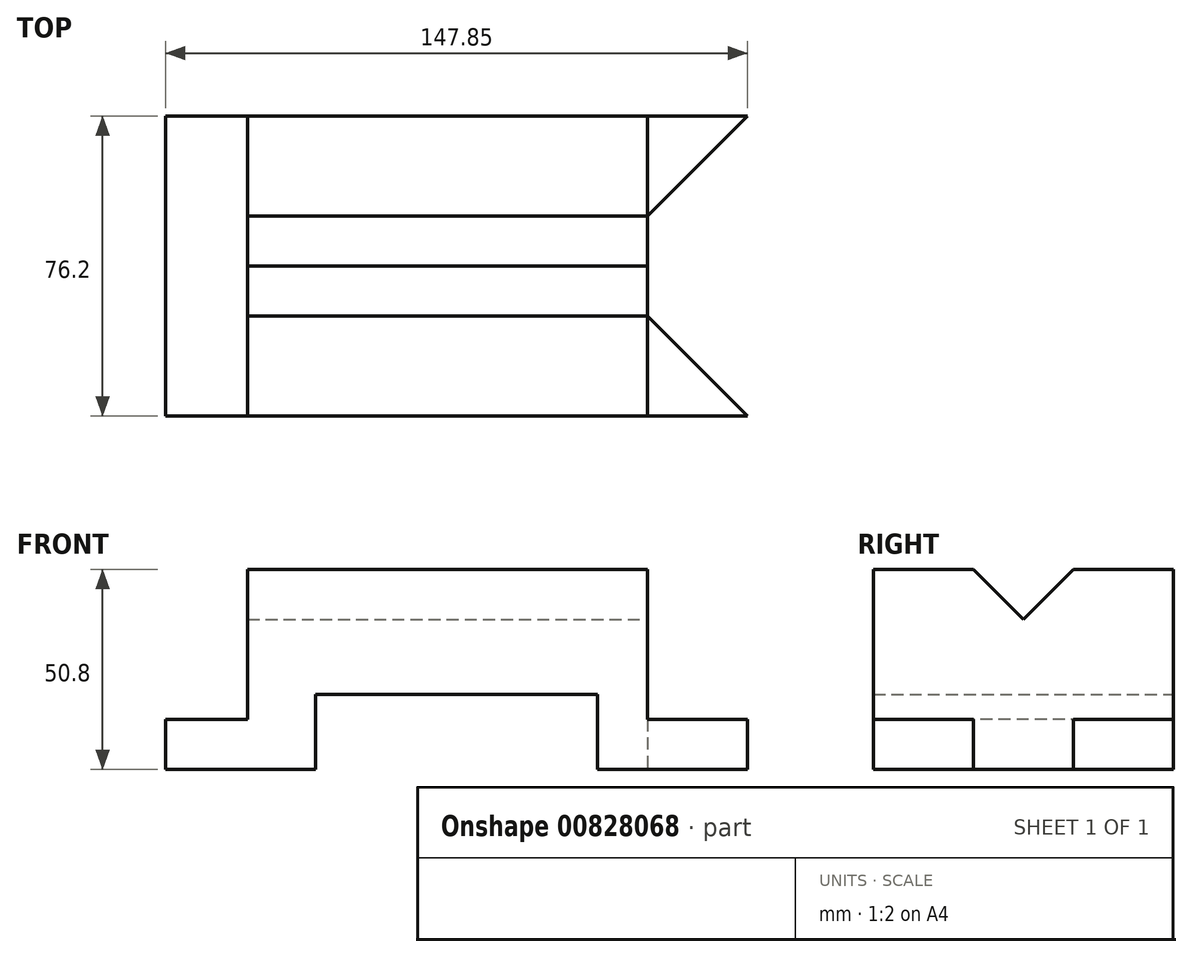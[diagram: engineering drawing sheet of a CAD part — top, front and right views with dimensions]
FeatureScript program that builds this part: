
annotation { "Feature Type Name" : "Feature", "Feature Type Description" : "" }
export const myFeature = defineFeature(function(context is Context, id is Id, definition is map)
    precondition{}
    {
        {
            var Q0;
            Q0=qCreatedBy(makeId("Top.planeOp"),FACE);
            var sketch = newSketch(context, id + "F0", { "sketchPlane" : qUnion([Q0])});
            skLineSegment(sketch, "E0", {"start": v(-51.86, 50.8) * mm, "end": v(-51.86, 54.53) * mm});
            skLineSegment(sketch, "E1", {"start": v(-51.86, 50.8) * mm, "end": v(-51.86, -25.4) * mm});
            skLineSegment(sketch, "E2", {"start": v(-51.86, -25.4) * mm, "end": v(49.74, -25.4) * mm});
            skLineSegment(sketch, "E3", {"start": v(49.74, -25.4) * mm, "end": v(49.74, 50.8) * mm});
            skLineSegment(sketch, "E4", {"start": v(49.74, 50.8) * mm, "end": v(-51.86, 50.8) * mm});
            skLineSegment(sketch, "E5", {"start": v(49.74, -25.4) * mm, "end": v(75.14, -25.4) * mm});
            skLineSegment(sketch, "E6", {"start": v(75.14, -25.4) * mm, "end": v(49.74, 0) * mm});
            skLineSegment(sketch, "E7", {"start": v(49.74, 50.8) * mm, "end": v(75.14, 50.8) * mm});
            skLineSegment(sketch, "E8", {"start": v(75.14, 50.8) * mm, "end": v(49.74, 25.4) * mm});
            skLineSegment(sketch, "E9", {"start": v(-51.86, 50.8) * mm, "end": v(-72.71, 50.8) * mm});
            skLineSegment(sketch, "E10", {"start": v(-72.71, 50.8) * mm, "end": v(-72.71, -25.4) * mm});
            skLineSegment(sketch, "E11", {"start": v(-72.71, -25.4) * mm, "end": v(-51.86, -25.4) * mm});
            skSolve(sketch);
        }
        {
            var Q0;
            Q0=makeQuery(id+"F0.imprint","IMPRINT",FACE,{"disambiguationData":[TD([[makeQuery(id+"F0.imprint","IMPRINT",EDGE,{"derivedFrom":sQuery(id+"F0.wireOp",EDGE,"E1")}),-1.0]])]});
            extrude(context, id + "F1", {"entities" : qUnion([Q0]), "depth" : 12.7 * mm, "offsetDistance" : 25.4 * mm});
        }
        {
            var Q0;
            Q0=makeQuery(id+"F0.imprint","IMPRINT",FACE,{"disambiguationData":[TD([[makeQuery(id+"F0.imprint","IMPRINT",EDGE,{"derivedFrom":sQuery(id+"F0.wireOp",EDGE,"E1")}),1.0]])]});
            extrude(context, id + "F2", {"entities" : qUnion([Q0]), "operationType" : NewBodyOperationType.ADD, "depth" : 50.8 * mm, "offsetDistance" : 25.4 * mm});
        }
        {
            var Q0;
            {var subQ0=sQuery(id+"F0.wireOp",EDGE,"E7");Q0=makeQuery(id+"F0.imprint","IMPRINT",FACE,{"disambiguationData":[TD([[makeQuery(id+"F0.imprint","IMPRINT",EDGE,{"derivedFrom":subQ0}),-1.0]])]});}
            extrude(context, id + "F3", {"entities" : qUnion([Q0]), "operationType" : NewBodyOperationType.ADD, "depth" : 12.7 * mm, "offsetDistance" : 25.4 * mm});
        }
        {
            var Q0;
            {var subQ0=sQuery(id+"F0.wireOp",EDGE,"E5");Q0=makeQuery(id+"F0.imprint","IMPRINT",FACE,{"disambiguationData":[TD([[makeQuery(id+"F0.imprint","IMPRINT",EDGE,{"derivedFrom":subQ0}),1.0]])]});}
            extrude(context, id + "F4", {"entities" : qUnion([Q0]), "operationType" : NewBodyOperationType.ADD, "depth" : 12.7 * mm, "offsetDistance" : 25.4 * mm});
        }
        {
            var Q0;
            Q0=makeQuery(id+"F2.opExtrude","SWEPT_FACE",FACE,{"disambiguationData":[OSD([sQuery(id+"F0.wireOp",EDGE,"E3")])]});
            var sketch = newSketch(context, id + "F5", { "sketchPlane" : qUnion([Q0])});
            skLineSegment(sketch, "E12", {"start": v(0, 50.8) * mm, "end": v(12.7, 38.1) * mm});
            skLineSegment(sketch, "E13", {"start": v(12.7, 38.1) * mm, "end": v(25.4, 50.8) * mm});
            skSolve(sketch);
        }
        {
            var Q0;
            {var subQ0=sQuery(id+"F5.wireOp",EDGE,"E12");Q0=makeQuery(id+"F5.imprint","IMPRINT",FACE,{"disambiguationData":[TD([[makeQuery(id+"F5.imprint","IMPRINT",EDGE,{"derivedFrom":subQ0}),1.0]])]});}
            extrude(context, id + "F6", {"entities" : qUnion([Q0]), "operationType" : NewBodyOperationType.REMOVE, "endBound" : BoundingType.THROUGH_ALL, "oppositeDirection" : true, "depth" : 25.4 * mm, "offsetDistance" : 25.4 * mm});
        }
        {
            var Q0;
            Q0=makeQuery(id+"F3.boolean.opBoolean","MERGE",FACE,{"derivedFrom":[makeQuery(id+"F2.boolean.opBoolean","MERGE",FACE,{"derivedFrom":[makeQuery(id+"F1.opExtrude","SWEPT_FACE",FACE,{"disambiguationData":[OSD([sQuery(id+"F0.wireOp",EDGE,"E9")])]}),makeQuery(id+"F2.opExtrude","SWEPT_FACE",FACE,{"disambiguationData":[OSD([sQuery(id+"F0.wireOp",EDGE,"E4")])]})]}),makeQuery(id+"F3.opExtrude","SWEPT_FACE",FACE,{"disambiguationData":[OSD([sQuery(id+"F0.wireOp",EDGE,"E7")])]})]});
            var sketch = newSketch(context, id + "F7", { "sketchPlane" : qUnion([Q0])});
            skLineSegment(sketch, "E14", {"start": v(-37.04, 0) * mm, "end": v(-37.04, 19.05) * mm});
            skLineSegment(sketch, "E15", {"start": v(34.61, 0) * mm, "end": v(34.61, 19.05) * mm});
            skLineSegment(sketch, "E16", {"start": v(-37.04, 19.05) * mm, "end": v(34.61, 19.05) * mm});
            skSolve(sketch);
        }
        {
            var Q0;
            {var subQ0=sQuery(id+"F7.wireOp",EDGE,"E14");Q0=makeQuery(id+"F7.imprint","IMPRINT",FACE,{"disambiguationData":[TD([[makeQuery(id+"F7.imprint","IMPRINT",EDGE,{"derivedFrom":subQ0}),-1.0]])]});}
            extrude(context, id + "F8", {"entities" : qUnion([Q0]), "operationType" : NewBodyOperationType.REMOVE, "oppositeDirection" : true, "depth" : 101.6 * mm, "offsetDistance" : 25.4 * mm});
        }
    });
